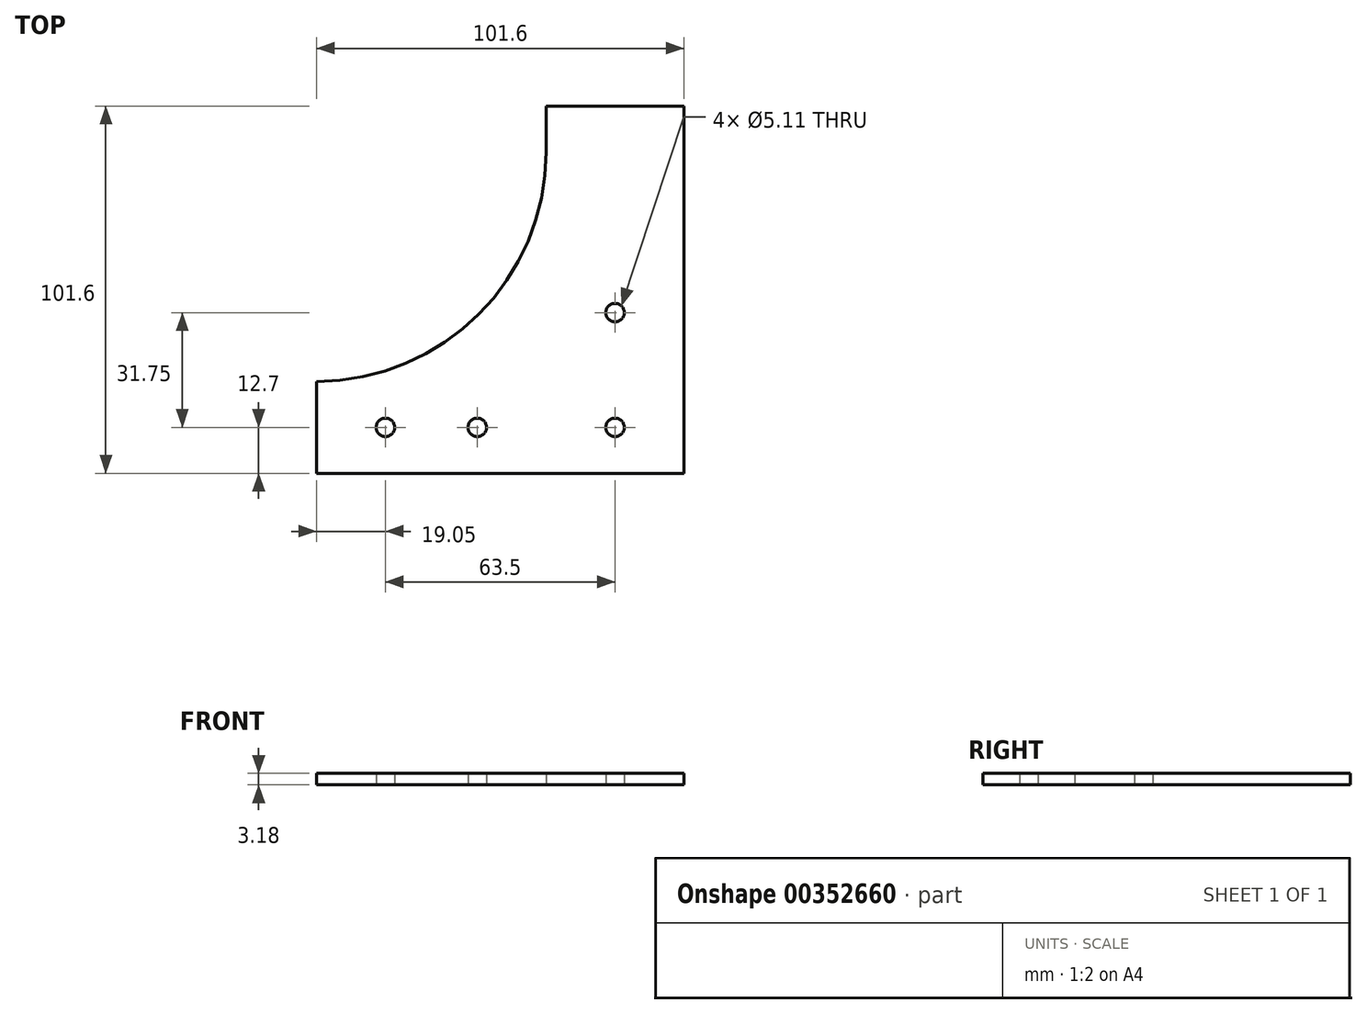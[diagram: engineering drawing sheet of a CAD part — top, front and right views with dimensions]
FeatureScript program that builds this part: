
annotation { "Feature Type Name" : "Feature", "Feature Type Description" : "" }
export const myFeature = defineFeature(function(context is Context, id is Id, definition is map)
    precondition{}
    {
        {
            var Q0;
            Q0=qCreatedBy(makeId("Top.planeOp"),FACE);
            var sketch = newSketch(context, id + "F0", { "sketchPlane" : qUnion([Q0])});
            skLineSegment(sketch, "E0", {"start": v(0, 0) * mm, "end": v(0, 101.6) * mm});
            skLineSegment(sketch, "E1", {"start": v(0, 0) * mm, "end": v(-101.6, 0) * mm});
            skLineSegment(sketch, "E2", {"start": v(-101.6, 0) * mm, "end": v(-101.6, 25.4) * mm});
            skLineSegment(sketch, "E3", {"start": v(0, 101.6) * mm, "end": v(-38.1, 101.6) * mm});
            skLineSegment(sketch, "E4", {"start": v(-38.1, 101.6) * mm, "end": v(-38.1, 25.4) * mm});
            skLineSegment(sketch, "E5", {"start": v(-38.1, 25.4) * mm, "end": v(-101.6, 25.4) * mm});
            skPoint(sketch, "E6", {"position": v(-82.55, 12.7) * mm});
            skPoint(sketch, "E7", {"position": v(-57.15, 12.7) * mm});
            skPoint(sketch, "E8", {"position": v(-19.05, 12.7) * mm});
            skPoint(sketch, "E9", {"position": v(-19.05, 44.45) * mm});
            skSolve(sketch);
        }
        {
            var Q0;
            Q0=makeQuery(id+"F0.imprint","IMPRINT",FACE,{"disambiguationData":[TD([[makeQuery(id+"F0.imprint","IMPRINT",EDGE,{"derivedFrom":sQuery(id+"F0.wireOp",EDGE,"E0")}),1.0]])]});
            extrude(context, id + "F1", {"entities" : qUnion([Q0]), "depth" : 3.17 * mm});
        }
        {
            var Q0;
            Q0=makeQuery(id+"F1.opExtrude","SWEPT_EDGE",EDGE,{"disambiguationData":[OSD([sQuery(id+"F0.wireOp",EDGE,"E4"),sQuery(id+"F0.wireOp",EDGE,"E5")])]});
            fillet(context, id + "F2", {"entities" : qUnion([Q0]), "radius" : 63.5 * mm, "tangentPropagation" : true, "allowEdgeOverflow" : false});
        }
        {
            var Q0;
            Q0=sQuery(id+"F0.wireOp",VERTEX,"E6");
            var Q1;
            Q1=sQuery(id+"F0.wireOp",VERTEX,"E7");
            var Q2;
            Q2=sQuery(id+"F0.wireOp",VERTEX,"E8");
            var Q3;
            Q3=sQuery(id+"F0.wireOp",VERTEX,"E9");
            var Q4;
            Q4=makeQuery(id+"F1.opExtrude","SWEPT_BODY",BODY,{"disambiguationData":[OSD([sQuery(id+"F0.wireOp",EDGE,"E0"),sQuery(id+"F0.wireOp",EDGE,"E1"),sQuery(id+"F0.wireOp",EDGE,"E2"),sQuery(id+"F0.wireOp",EDGE,"E3"),sQuery(id+"F0.wireOp",EDGE,"E4"),sQuery(id+"F0.wireOp",EDGE,"E5")])]});
            hole(context, id + "F3", {"style" : HoleStyle.SIMPLE, "endStyle" : HoleEndStyle.THROUGH, "oppositeDirection" : true, "holeDiameter" : 5.1 * mm, "isTappedThrough" : true, "tappedDepth" : 12.7 * mm, "tapClearance" : 3, "locations" : qUnion([Q0, Q1, Q2, Q3]), "scope" : qUnion([Q4])});
        }
    });
